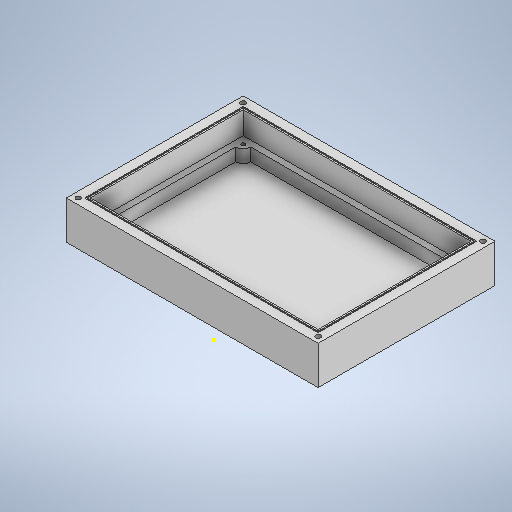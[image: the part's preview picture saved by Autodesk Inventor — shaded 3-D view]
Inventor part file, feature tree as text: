
AUTODESK INVENTOR PART (.ipt)
format: ipt  version: 2025.1 (Build 291241000, 241)  size: 527,360 bytes
history: native  units: mm
features: sketch x13, hole x6, extrude x5, shell x1
ambient origin geometry x8: Origin, YZ Plane, XZ Plane, XY Plane, X Axis, Y Axis, Z Axis, Center Point
bodies: Body1 (feature_tree)
feature tree (25):
  extrude  "Extrusão7"  Depth=102.0mm
  shell  "Casca2"  Thickness=10.6mm
  extrude  "Extrusão8"  Depth=8.0mm
  extrude  "Extrusão9"  Depth=8.0mm
  extrude  "Extrusão10"  Depth=15.0mm TaperAngle=0.0deg
  hole  "Furo2"  [1 undecoded]
  hole  "Furo3"  [1 undecoded]
  hole  "Furo4"  [1 undecoded]
  hole  "Furo5"  [1 undecoded]
  sketch  "Esboço18"  dims[d64=5.0mm d65=8.6mm d66=0.0mm]
  sketch  "Esboço19"  dims[d67=5.0mm d68=5.0mm]
  hole  "Furo6"  [1 undecoded]
  extrude  "Extrusão11"  Depth=5.0mm
  hole  "Furo7"  [1 undecoded]
  sketch  "Esboço9"  dims[d42=152.0mm d43=102.0mm d44=10.6mm d45=0.0mm]
  sketch  "Esboço10"  dims[d46=2.0mm d47=8.0mm]
  sketch  "Esboço11"  dims[d48=8.0mm d49=8.0mm]
  sketch  "Esboço12"  dims[d50=8.0mm d51=15.0mm d52=10.6mm d53=0.0mm d54=0.0mm]
  sketch  "Esboço13"  dims[d55=2.0mm d56=2.0mm]
  sketch  "Esboço14"  dims[d57=2.0mm d58=2.0mm]
  sketch  "Esboço15"  dims[d59=8.6mm d60=0.0mm d61=5.0mm]
  sketch  "Esboço16"  dims[d62=5.0mm d63=5.0mm]
  sketch  "Esboço20"  dims[d69=2.459mm d70=4.0mm d71=4.0mm d72=2.0mm d73=90.0deg d74=5.0mm d75=20.594885mm d76=5.0mm]
  sketch  "Esboço21"  dims[d77=5.0mm]
  sketch  "Esboço22"  dims[d78=2.459mm d79=4.0mm d80=4.0mm d81=2.0mm d82=90.0deg d83=5.0mm d84=20.594885mm d85=5.0mm d86=5.0mm d87=2.459mm d88=4.0mm d89=4.0mm d90=2.0mm d91=90.0deg d92=5.0mm d93=20.594885mm d94=5.0mm d95=5.0mm d96=2.459mm d97=4.0mm d98=4.0mm d99=2.0mm d100=90.0deg d101=5.0mm d102=20.594885mm d104=4.0mm d105=4.0mm d106=3.242mm d107=10.0mm d108=4.0mm d109=2.0mm d110=90.0deg d111=15.0mm d112=20.594885mm d117=0.9mm d118=0.4mm d119=0.6mm d120=0.0mm d121=4.0mm d122=4.0mm d123=4.0mm d124=4.0mm d125=4.0mm d126=4.0mm d127=3.242mm d128=10.0mm d129=4.0mm d130=2.0mm d131=90.0deg d132=15.0mm d133=20.594885mm d0=0.5mm d1=0.872665mm d2=0.5mm d3=0.872665mm d39=0.0mm d40=0.0mm d41=0.0mm]
note: 6 required parameter values undecoded (feature->parameter linkage not recoverable at this tier; creation-order binding heuristic only, values carry confidence <= 0.55)
